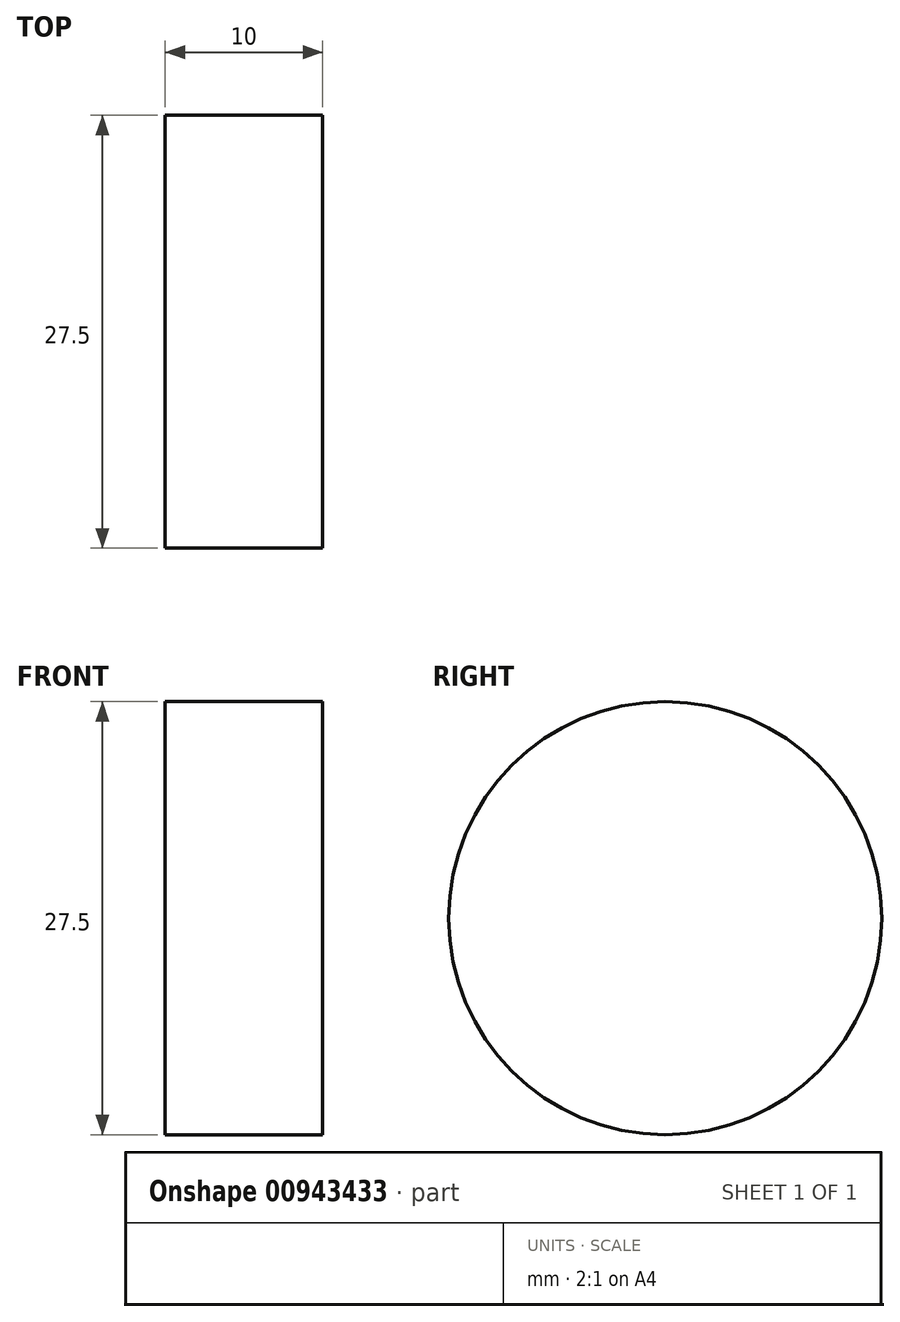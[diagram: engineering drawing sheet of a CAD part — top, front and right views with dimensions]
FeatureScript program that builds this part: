
annotation { "Feature Type Name" : "Feature", "Feature Type Description" : "" }
export const myFeature = defineFeature(function(context is Context, id is Id, definition is map)
    precondition{}
    {
        {
            var Q0;
            Q0=qCreatedBy(makeId("Right.planeOp"),FACE);
            var sketch = newSketch(context, id + "F0", { "sketchPlane" : qUnion([Q0])});
            skCircle(sketch, "E0", {"center": v(0, 0) * mm, "radius": 13.75 * mm});
            skSolve(sketch);
        }
        {
            var Q0;
            Q0=makeQuery(id+"F0.imprint","IMPRINT",FACE,{"disambiguationData":[TD([[makeQuery(id+"F0.imprint","IMPRINT",EDGE,{"derivedFrom":sQuery(id+"F0.wireOp",EDGE,"E0")}),1.0]])]});
            extrude(context, id + "F1", {"entities" : qUnion([Q0]), "depth" : 10 * mm, "offsetDistance" : 25.4 * mm});
        }
    });
